# Revit family: r2018_videomax_jbod
name_source: partatom
category: Устройства связи
revit_build: Autodesk Revit 2018 (Build: 20181011_1500(x64)
units: mm (PartAtom-declared; Revit-internal decimal feet)

## family parameters
Общий = Нет
Основа = Грань
При загрузке вырезать с полостями = Нет
Размер круглого соединителя = Использовать диаметр
Сохранять ориентацию аннотаций = Да
Тип детали = Нормальный
Точка расчета площади = Нет

## types (3) — shared parameters
ADSK_Версия Revit = 2018
ADSK_Версия семейства = v2
ADSK_Единица измерения = шт.
ADSK_Количество = 1
ADSK_Коэффициент мощности = 0.96
ADSK_Напряжение = 230 В
ADSK_Номинальная мощность = 0 В·А
ADSK_Ток = 0 А
Maaterial = Черный
URL = https://www.videomax-server.ru
Глубина = 430 мм
Изготовитель = ООО «Видеомакс»
Количество входов 230V, шт = 2
Минимальная глубина шкафа = 1000
Отметка по умолчанию = 2600 мм
Указания по монтажу = Для монтажа использовать комплектные 19” салазки с параметрами: расстояние между профилями 646 - 940 мм, габариты в сложенном состоянии 757 мм.
Ширина = 534 мм
zero-valued in all types: ADSK_Масса, Максимальная мощность БП, Вт, Максимальная потребляемая мощность Вт, Максимальное тепловыделение, BTU/h, Стоимость

## per-type parameters (varying)
| type | 19” 2U (JBOD) | 19” 3U (JBOD) | 19” 4U (JBOD) | ADSK_Наименование | Back | Front | Высота | Высота в U | Изображение типоразмера |
| 19” 3U (JBOD) | Нет | Да | Нет | Дополнительный накопитель 19” 3U | videomax_19 3U (JBOD) : Back | videomax_19 3U (JBOD) : Front | 133 мм | 3 | 19 (3U) Short.png |
| 19” 4U (JBOD) | Нет | Нет | Да | Дополнительный накопитель 19” 4U | videomax_19 4U (JBOD) : Back | videomax_19 4U (JBOD) : Front | 176 мм | 4 | 19 (4U) Short.png |
| 19” 2U (JBOD) | Да | Нет | Нет | Дополнительный накопитель 19” 2U | videomax_19 2U (JBOD) : Back | videomax_19 2U (JBOD) : Front | 88 мм | 2 | 19 (2U) Short.png |

note: column(s) folded — value = type name in every type: ADSK_Обозначение
